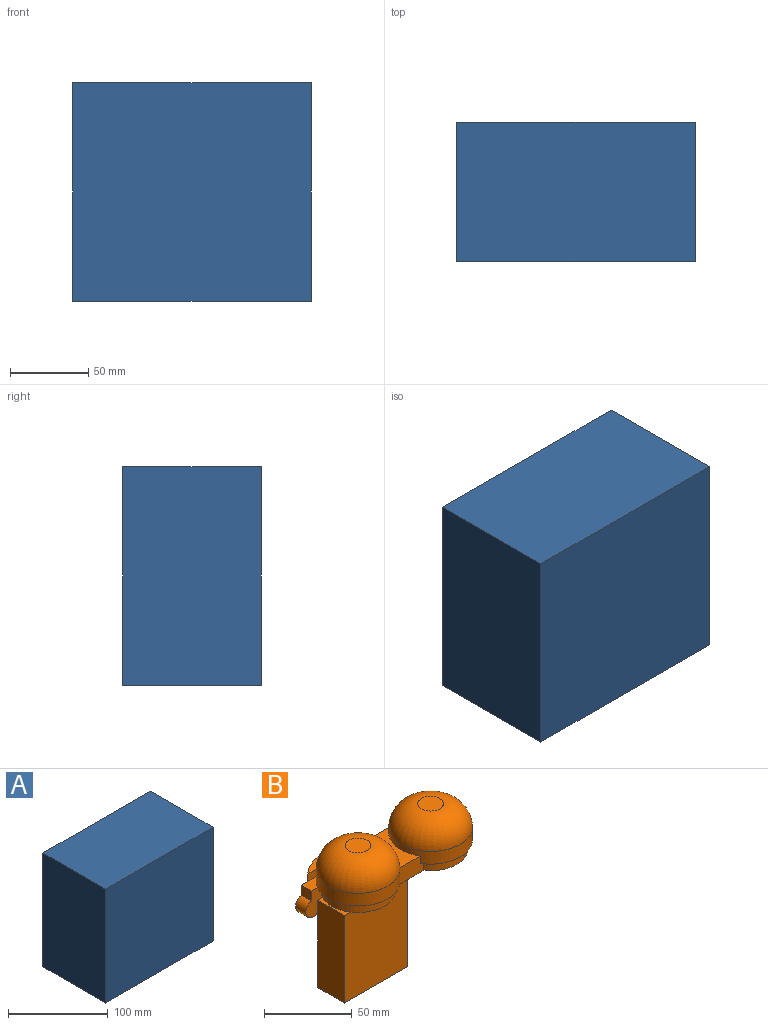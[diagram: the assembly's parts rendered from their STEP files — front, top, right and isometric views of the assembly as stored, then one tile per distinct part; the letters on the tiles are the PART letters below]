
ASSEMBLY  parts=2 mates=1
PART A: 13 faces, bbox 152.4x88.9x139.7 mm
  f0: plane 152.4x88.9mm, normal (0,0,-1), area 4677.4mm2, adj f2,f4,f5,f6,f7,f8,f9,f10
  f1: plane 127x88.9mm, normal (0,-1,0), area 11290.3mm2, adj f3,f5,f8,f11
  f2: plane 152.4x139.7mm, normal (0,1,0), area 21290.3mm2, adj f0,f6,f7,f12
  f3: plane 127x6.35mm, normal (0,0,-1), area 806.5mm2, adj f1,f4,f5,f8
  f4: plane 127x38.1mm, normal (0,-1,0), area 4838.7mm2, adj f0,f3,f5,f8
  f5: plane 127x69.85mm, normal (-1,0,0), area 8306.4mm2, adj f0,f1,f3,f4,f9,f11
  f6: plane 139.7x88.9mm, normal (1,0,0), area 12419.3mm2, adj f0,f2,f10,f12
  f7: plane 139.7x88.9mm, normal (-1,0,0), area 12419.3mm2, adj f0,f2,f10,f12
  f8: plane 127x69.85mm, normal (1,0,0), area 8306.4mm2, adj f0,f1,f3,f4,f9,f11
  f9: plane 127x127mm, normal (0,1,0), area 16129mm2, adj f0,f5,f8,f11
  f10: plane 152.4x139.7mm, normal (0,-1,0), area 21290.3mm2, adj f0,f6,f7,f12
  f11: plane 127x63.5mm, normal (0,0,-1), area 8064.5mm2, adj f1,f5,f8,f9
  f12: plane 152.4x88.9mm, normal (0,0,1), area 13548.4mm2, adj f2,f6,f7,f10
PART B: 47 faces, bbox 118.4x52.5x95.3 mm
  f0: plane 44.31x34.51mm, normal (0,0,-1), area 165.7mm2, adj f1,f6,f7,f8
  f1: cylinder r=23.81mm len=47.63mm, axis (0,0,-1), area 1068.2mm2, adj f0,f3,f4,f5,f6,f7,f9,f20
  f2: plane 14.61x14.61mm, normal (0,0,1), area 167.5mm2, adj f4
  f3: plane 23.76x3.18mm, normal (0,0,-1), area 51mm2, adj f1,f9
  f4: torus R=7.3mm, axis (0,0,1), area 2902.6mm2, adj f1,f2
  f5: plane 9.94x9.39mm, normal (0,0,1), area 37.5mm2, adj f1,f7,f9
  f6: plane 23.47x11.43mm, normal (0,-1,0), area 237.6mm2, adj f0,f1,f8,f10,f11,f16,f17,f20
  f7: plane 20.64x11.43mm, normal (1,0,0), area 129.1mm2, adj f0,f1,f5,f8,f9,f17,f44,f46
  f8: cylinder r=21.27mm len=38.75mm, axis (0,0,-1), area 342.4mm2, adj f0,f6,f7,f17
  f9: plane 118.36x74.93mm, normal (0,1,0), area 2244.4mm2, adj f1,f3,f5,f7,f14,f17,f18,f19
  f10: cylinder r=23.81mm len=47.63mm, axis (0,0,-1), area 1012.3mm2, adj f6,f11,f13,f14,f15,f20
  f11: plane 44.31x36.2mm, normal (0,0,-1), area 180.7mm2, adj f6,f10,f16,f42
  f12: plane 14.61x14.61mm, normal (0,0,1), area 167.5mm2, adj f13
  f13: torus R=7.3mm, axis (0,0,1), area 2902.6mm2, adj f10,f12
  f14: plane 13.46x8.26mm, normal (0,0,1), area 70.3mm2, adj f9,f10,f15,f26,f42
  f15: plane 8.01x5.08mm, normal (0,-1,0), area 40.7mm2, adj f10,f14,f19,f20
  f16: cylinder r=21.27mm len=38.75mm, axis (0,0,-1), area 426.3mm2, adj f6,f11,f17,f42
  f17: plane 100.97x41.91mm, normal (0,0,-1), area 3162.1mm2, adj f6,f7,f8,f9,f16,f42,f43,f45
  f18: plane 39.79x8.03mm, normal (0,0,-1), area 219.7mm2, adj f9,f19
  f19: cylinder r=28.66mm len=39.79mm, axis (0,0,-1), area 502.6mm2, adj f9,f15,f18,f20
  f20: plane 66.43x40.79mm, normal (0,0,1), area 691.6mm2, adj f1,f6,f9,f10,f15,f19
  f21: plane 60.96x50.8mm, normal (0,-1,0), area 3096.8mm2, adj f22,f23,f24,f32
  f22: plane 60.96x21.59mm, normal (-1,0,0), area 1316.1mm2, adj f21,f23,f25,f32,f42
  f23: plane 50.8x21.59mm, normal (0,0,1), area 1096.8mm2, adj f21,f22,f24,f42
  f24: plane 60.96x21.59mm, normal (1,0,0), area 1316.1mm2, adj f21,f23,f32,f42
  f25: plane 57.15x41.53mm, normal (0,1,0), area 1995.7mm2, adj f22,f32,f33,f34,f35,f36,f37,f38
  f26: plane 8.26x6.92mm, normal (-1,0,0), area 57.1mm2, adj f9,f14,f41,f42
  f27: plane 10.1x8.26mm, normal (0.91,0,-0.42), area 92mm2, adj f9,f28,f42,f43
  f28: plane 38.1x8.26mm, normal (1,0,0), area 314.5mm2, adj f9,f27,f29,f42
  f29: plane 8.26x5.59mm, normal (0,0,1), area 46.1mm2, adj f9,f28,f30,f42
  f30: plane 8.26x6.99mm, normal (1,0,0), area 57.7mm2, adj f9,f29,f31,f42
  f31: cylinder r=3.17mm len=8.26mm, axis (0,1,0), area 41.2mm2, adj f9,f30,f32,f42
  f32: plane 54.86x29.85mm, normal (0,0,-1), area 1468.9mm2, adj f9,f21,f22,f24,f25,f31,f33,f42
  f33: plane 8.26x7.87mm, normal (-1,0,0), area 65mm2, adj f9,f25,f32,f34
  f34: plane 19.05x8.26mm, normal (0,0,1), area 157.3mm2, adj f9,f25,f33,f35
  f35: plane 8.26x8mm, normal (-1,0,0), area 66mm2, adj f9,f25,f34,f36
  f36: plane 8.26x6.35mm, normal (0,0,1), area 52.4mm2, adj f9,f25,f35,f37
  f37: cylinder r=6.35mm len=8.26mm, axis (0,1,0), area 82.3mm2, adj f9,f25,f36,f38
  f38: plane 28.58x8.26mm, normal (-1,0,0), area 235.9mm2, adj f9,f25,f37,f39
  f39: cylinder r=6.35mm len=8.26mm, axis (0,1,0), area 82.3mm2, adj f9,f25,f38,f40
  f40: plane 32.64x8.26mm, normal (0,0,-1), area 269.4mm2, adj f9,f25,f39,f41
  f41: cylinder r=6.03mm len=12.07mm, axis (0,1,0), area 220.3mm2, adj f9,f25,f26,f40,f42
  f42: plane 72.07x69.85mm, normal (0,-1,0), area 497.7mm2, adj f11,f14,f16,f17,f22,f23,f24,f26
  f43: cylinder r=10.22mm len=8.26mm, axis (0,1,0), area 62.9mm2, adj f9,f17,f27,f42
  f44: plane 8.26x0.95mm, normal (0,0,1), area 7.8mm2, adj f7,f9,f45,f46
  f45: cylinder r=5.97mm len=11.94mm, axis (0,1,0), area 243.6mm2, adj f9,f17,f44,f46
  f46: plane 11.94x11.89mm, normal (0,-1,0), area 99.3mm2, adj f7,f17,f44,f45
PLACE A t=(27.45,11.53,3.05)mm fixed
PLACE B rot(axis=(0,1,0),180deg) t=(23.35,-1.17,-26.56)mm
MATE planar B.f9 <-> A.f1  axis (0,1,0) through (35.54,-1.17,21.07)mm
